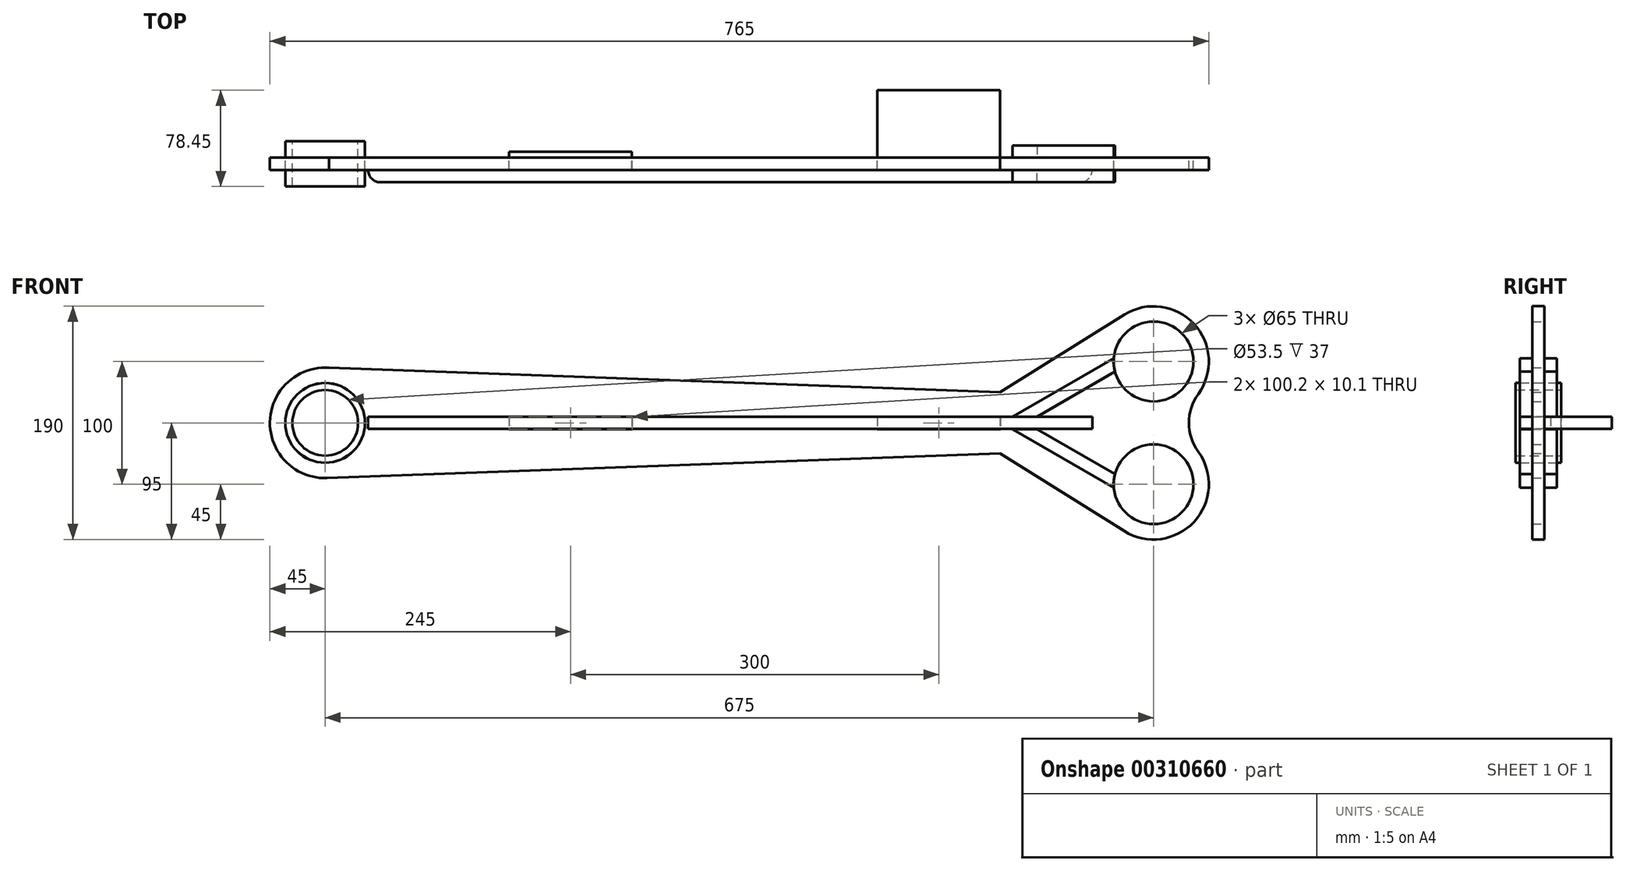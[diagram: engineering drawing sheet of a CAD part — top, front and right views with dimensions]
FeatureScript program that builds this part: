
annotation { "Feature Type Name" : "Feature", "Feature Type Description" : "" }
export const myFeature = defineFeature(function(context is Context, id is Id, definition is map)
    precondition{}
    {
        {
            var Q0;
            Q0=qCreatedBy(makeId("Front.planeOp"),FACE);
            var sketch = newSketch(context, id + "F0", { "sketchPlane" : qUnion([Q0])});
            skCircle(sketch, "E0", {"center": v(0, 0) * mm, "radius": 32.5 * mm});
            skCircle(sketch, "E1", {"center": v(0, 0) * mm, "radius": 45 * mm});
            skCircle(sketch, "E2", {"center": v(750, 0) * mm, "radius": 32.5 * mm, "construction": true});
            skCircle(sketch, "E3", {"center": v(675, 50) * mm, "radius": 32.5 * mm});
            skCircle(sketch, "E4", {"center": v(675, -50) * mm, "radius": 32.5 * mm});
            skCircle(sketch, "E5", {"center": v(675, 50) * mm, "radius": 45 * mm});
            skArc(sketch, "E6", {"start": v(651.17, -88.17) * mm, "mid": v(707.92, -80.68) * mm, "end": v(711.4, -23.53) * mm});
            skLineSegment(sketch, "E7", {"start": v(550, 25) * mm, "end": v(550, -25) * mm, "construction": true});
            skPoint(sketch, "E8", {"position": v(550, 0) * mm});
            skLineSegment(sketch, "E9", {"start": v(0, 45) * mm, "end": v(550, 25) * mm});
            skLineSegment(sketch, "E10", {"start": v(550, -25) * mm, "end": v(0, -45.03) * mm});
            skLineSegment(sketch, "E11", {"start": v(550, 25) * mm, "end": v(651.17, 88.17) * mm});
            skLineSegment(sketch, "E12", {"start": v(550, -25) * mm, "end": v(651.17, -88.17) * mm});
            skArc(sketch, "E13", {"start": v(711.4, 23.53) * mm, "mid": v(703.74, 0) * mm, "end": v(711.4, -23.53) * mm});
            skLineSegment(sketch, "E14.bottom", {"start": v(149.9, 5.05) * mm, "end": v(250.1, 5.05) * mm});
            skLineSegment(sketch, "E14.top", {"start": v(149.9, -5.05) * mm, "end": v(250.1, -5.05) * mm});
            skLineSegment(sketch, "E14.left", {"start": v(149.9, 5.05) * mm, "end": v(149.9, -5.05) * mm});
            skLineSegment(sketch, "E14.right", {"start": v(250.1, 5.05) * mm, "end": v(250.1, -5.05) * mm});
            skLineSegment(sketch, "E15.bottom", {"start": v(449.9, 5.05) * mm, "end": v(550.1, 5.05) * mm});
            skLineSegment(sketch, "E15.top", {"start": v(449.9, -5.05) * mm, "end": v(550.1, -5.05) * mm});
            skLineSegment(sketch, "E15.left", {"start": v(449.9, 5.05) * mm, "end": v(449.9, -5.05) * mm});
            skLineSegment(sketch, "E15.right", {"start": v(550.1, 5.05) * mm, "end": v(550.1, -5.05) * mm});
            skSolve(sketch);
        }
        {
            var Q0;
            Q0=qSketchRegion(id+"F0",true);
            extrude(context, id + "F1", {"entities" : qUnion([Q0]), "depth" : 5 * mm, "hasSecondDirection" : true, "secondDirectionOppositeDirection" : true, "secondDirectionDepth" : 5 * mm});
        }
        {
            var Q0;
            Q0=qCreatedBy(makeId("Top.planeOp"),FACE);
            var sketch = newSketch(context, id + "F2", { "sketchPlane" : qUnion([Q0])});
            skLineSegment(sketch, "E16", {"start": v(35, -5.05) * mm, "end": v(35, -5.05) * mm});
            skLineSegment(sketch, "E17", {"start": v(45, -15.05) * mm, "end": v(615, -15.05) * mm});
            skLineSegment(sketch, "E18", {"start": v(625, -5.05) * mm, "end": v(625, -5.05) * mm});
            skLineSegment(sketch, "E19", {"start": v(625, -5.05) * mm, "end": v(550, -5.05) * mm});
            skLineSegment(sketch, "E20.trimOffspring", {"start": v(150, -5.05) * mm, "end": v(35, -5.05) * mm});
            skLineSegment(sketch, "E21", {"start": v(450, -5.05) * mm, "end": v(450, 59.95) * mm});
            skLineSegment(sketch, "E22", {"start": v(550, 59.95) * mm, "end": v(550, -5.05) * mm});
            skPoint(sketch, "E23.visualSharp", {"position": v(625, -15.05) * mm});
            skArc(sketch, "E23.filletArc", {"start": v(615, -15.05) * mm, "mid": v(622.07, -12.12) * mm, "end": v(625, -5.05) * mm});
            skPoint(sketch, "E24.visualSharp", {"position": v(35, -15.05) * mm});
            skArc(sketch, "E24.filletArc", {"start": v(35, -5.05) * mm, "mid": v(37.93, -12.12) * mm, "end": v(45, -15.05) * mm});
            skLineSegment(sketch, "E25.top", {"start": v(150, 9.95) * mm, "end": v(250, 9.95) * mm});
            skLineSegment(sketch, "E25.left", {"start": v(150, -5.05) * mm, "end": v(150, 9.95) * mm});
            skLineSegment(sketch, "E25.right", {"start": v(250, -5.05) * mm, "end": v(250, 9.95) * mm});
            skLineSegment(sketch, "E26", {"start": v(450, 59.95) * mm, "end": v(550, 59.95) * mm});
            skLineSegment(sketch, "E27.trimOffspring", {"start": v(450, -5.05) * mm, "end": v(250, -5.05) * mm});
            skSolve(sketch);
        }
        {
            var Q0;
            Q0=qSketchRegion(id+"F2",true);
            extrude(context, id + "F3", {"entities" : qUnion([Q0]), "depth" : 5 * mm, "hasSecondDirection" : true, "secondDirectionOppositeDirection" : true, "secondDirectionDepth" : 5 * mm});
        }
        {
            var Q0;
            Q0=makeQuery(id+"F1.opExtrude","CAP_FACE",FACE,{"disambiguationData":[OSD([sQuery(id+"F0.wireOp",EDGE,"E0"),sQuery(id+"F0.wireOp",EDGE,"E1"),sQuery(id+"F0.wireOp",EDGE,"E3"),sQuery(id+"F0.wireOp",EDGE,"E4"),sQuery(id+"F0.wireOp",EDGE,"E5"),sQuery(id+"F0.wireOp",EDGE,"E6"),sQuery(id+"F0.wireOp",EDGE,"E9"),sQuery(id+"F0.wireOp",EDGE,"E10"),sQuery(id+"F0.wireOp",EDGE,"E11"),sQuery(id+"F0.wireOp",EDGE,"E12"),sQuery(id+"F0.wireOp",EDGE,"E13"),sQuery(id+"F0.wireOp",EDGE,"E14.bottom"),sQuery(id+"F0.wireOp",EDGE,"E14.top"),sQuery(id+"F0.wireOp",EDGE,"E14.left"),sQuery(id+"F0.wireOp",EDGE,"E14.right"),sQuery(id+"F0.wireOp",EDGE,"E15.bottom"),sQuery(id+"F0.wireOp",EDGE,"E15.top"),sQuery(id+"F0.wireOp",EDGE,"E15.left"),sQuery(id+"F0.wireOp",EDGE,"E15.right")])],"isStart":true});
            var sketch = newSketch(context, id + "F4", { "sketchPlane" : qUnion([Q0])});
            skLineSegment(sketch, "E28", {"start": v(-643.46, -41.74) * mm, "end": v(-580, -5.1) * mm});
            skLineSegment(sketch, "E29", {"start": v(-580, -5.1) * mm, "end": v(-560, -5.1) * mm});
            skLineSegment(sketch, "E30", {"start": v(-560, -5.1) * mm, "end": v(-642.52, -52.74) * mm});
            skCircle(sketch, "E31", {"center": v(-675, -50) * mm, "radius": 32.6 * mm, "construction": true});
            skArc(sketch, "E32", {"start": v(-642.52, -52.74) * mm, "mid": v(-642.52, -47.2) * mm, "end": v(-643.46, -41.74) * mm});
            skLineSegment(sketch, "E33.MirrorCS", {"start": v(-580, 5.1) * mm, "end": v(-560, 5.1) * mm});
            skArc(sketch, "E34.MirrorCS", {"start": v(-642.52, 52.74) * mm, "mid": v(-642.52, 47.2) * mm, "end": v(-643.46, 41.74) * mm});
            skLineSegment(sketch, "E35.MirrorCS", {"start": v(-643.46, 41.74) * mm, "end": v(-580, 5.1) * mm});
            skLineSegment(sketch, "E36.MirrorCS", {"start": v(-560, 5.1) * mm, "end": v(-642.52, 52.74) * mm});
            skSolve(sketch);
        }
        {
            var Q0;
            Q0=qSketchRegion(id+"F4",true);
            extrude(context, id + "F5", {"entities" : qUnion([Q0]), "depth" : 10 * mm});
        }
        {
            var Q0;
            Q0=makeQuery(id+"F5.opExtrude","SWEPT_BODY",BODY,{"disambiguationData":[OSD([sQuery(id+"F4.wireOp",EDGE,"E33.MirrorCS"),sQuery(id+"F4.wireOp",EDGE,"E34.MirrorCS"),sQuery(id+"F4.wireOp",EDGE,"E35.MirrorCS"),sQuery(id+"F4.wireOp",EDGE,"E36.MirrorCS")])]});
            var Q1;
            Q1=makeQuery(id+"F5.opExtrude","SWEPT_BODY",BODY,{"disambiguationData":[OSD([sQuery(id+"F4.wireOp",EDGE,"E28"),sQuery(id+"F4.wireOp",EDGE,"E29"),sQuery(id+"F4.wireOp",EDGE,"E30"),sQuery(id+"F4.wireOp",EDGE,"E32")])]});
            var Q2;
            Q2=qCreatedBy(makeId("Front.planeOp"),FACE);
            mirror(context, id + "F6", {"entities" : qUnion([Q0, Q1]), "mirrorPlane" : qUnion([Q2])});
        }
        {
            var Q0;
            Q0=qCreatedBy(makeId("Front.planeOp"),FACE);
            var sketch = newSketch(context, id + "F7", { "sketchPlane" : qUnion([Q0])});
            skCircle(sketch, "E37", {"center": v(0, 0) * mm, "radius": 32.45 * mm});
            skCircle(sketch, "E38", {"center": v(0, 0) * mm, "radius": 26.75 * mm});
            skSolve(sketch);
        }
        {
            var Q0;
            Q0=qSketchRegion(id+"F7",true);
            extrude(context, id + "F8", {"entities" : qUnion([Q0]), "depth" : 18.5 * mm, "hasSecondDirection" : true, "secondDirectionOppositeDirection" : true, "secondDirectionDepth" : 18.5 * mm});
        }
    });
